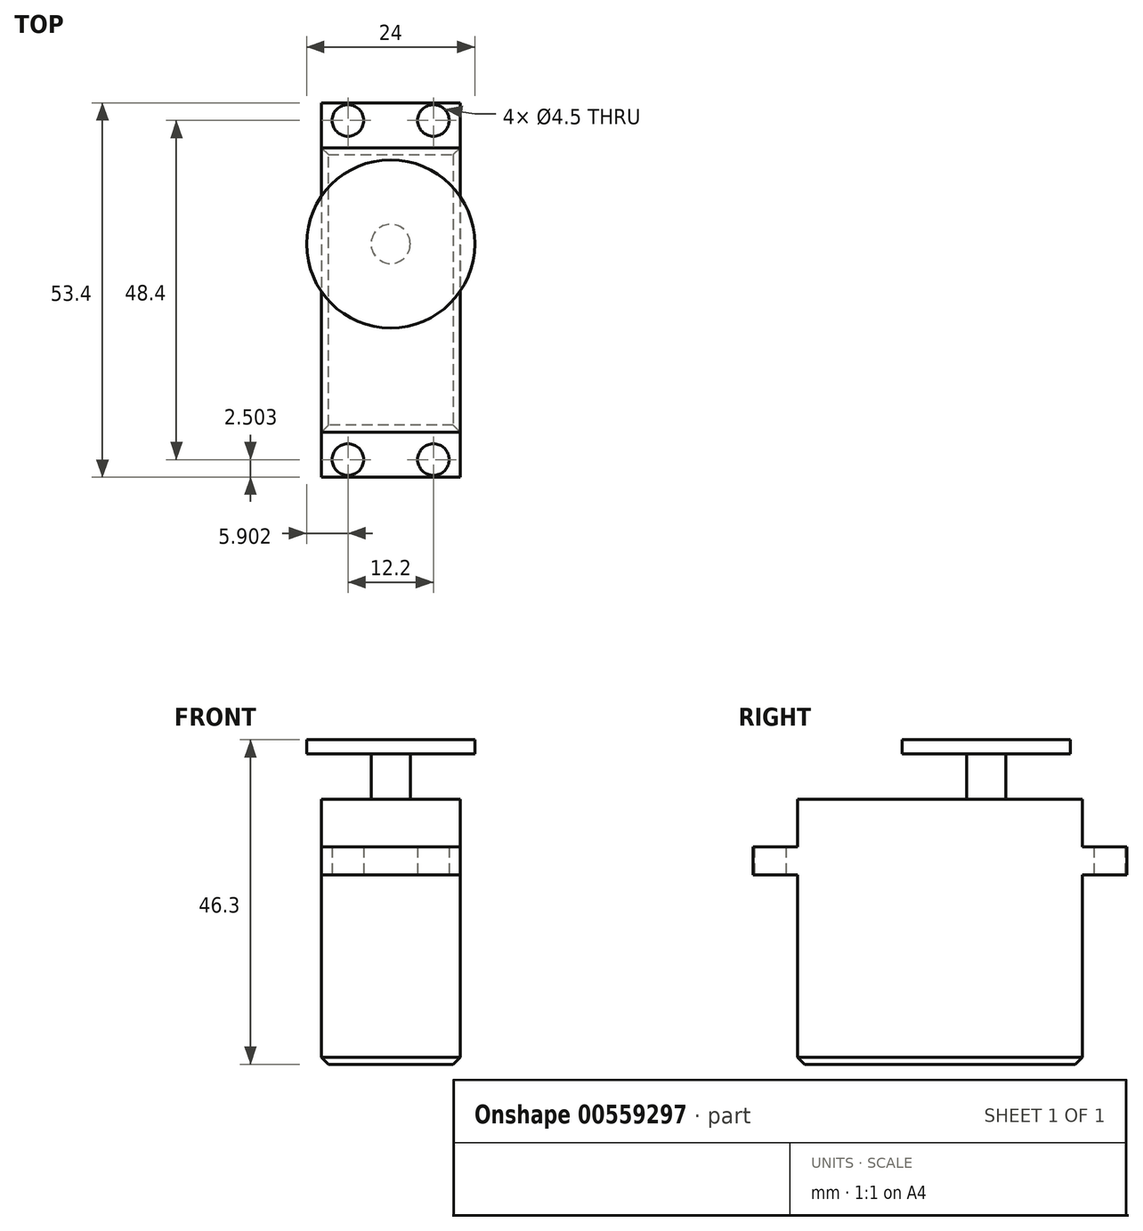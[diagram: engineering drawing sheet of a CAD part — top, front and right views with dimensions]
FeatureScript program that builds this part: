
annotation { "Feature Type Name" : "Feature", "Feature Type Description" : "" }
export const myFeature = defineFeature(function(context is Context, id is Id, definition is map)
    precondition{}
    {
        {
            var Q0;
            Q0=qCreatedBy(makeId("Top.planeOp"),FACE);
            var sketch = newSketch(context, id + "F0", { "sketchPlane" : qUnion([Q0])});
            skLineSegment(sketch, "E0.bottom", {"start": v(-14.2, 14.35) * mm, "end": v(5.6, 14.35) * mm});
            skLineSegment(sketch, "E0.top", {"start": v(-14.2, -26.25) * mm, "end": v(5.6, -26.25) * mm});
            skLineSegment(sketch, "E0.left", {"start": v(-14.2, 14.35) * mm, "end": v(-14.2, -26.25) * mm});
            skLineSegment(sketch, "E0.right", {"start": v(5.6, 14.35) * mm, "end": v(5.6, -26.25) * mm});
            skSolve(sketch);
        }
        {
            var Q0;
            Q0=makeQuery(id+"F0.imprint","IMPRINT",FACE,{"disambiguationData":[TD([[makeQuery(id+"F0.imprint","IMPRINT",EDGE,{"derivedFrom":sQuery(id+"F0.wireOp",EDGE,"E0.bottom")}),-1.0]])]});
            extrude(context, id + "F1", {"entities" : qUnion([Q0]), "depth" : 27 * mm, "offsetDistance" : 25 * mm});
        }
        {
            var Q0;
            Q0=makeQuery(id+"F1.opExtrude","CAP_FACE",FACE,{"disambiguationData":[OSD([sQuery(id+"F0.wireOp",EDGE,"E0.bottom"),sQuery(id+"F0.wireOp",EDGE,"E0.top"),sQuery(id+"F0.wireOp",EDGE,"E0.left"),sQuery(id+"F0.wireOp",EDGE,"E0.right")])],"isStart":false});
            var sketch = newSketch(context, id + "F2", { "sketchPlane" : qUnion([Q0])});
            skLineSegment(sketch, "E1", {"start": v(-14.2, 14.35) * mm, "end": v(-14.2, 20.75) * mm});
            skLineSegment(sketch, "E2", {"start": v(-14.2, 20.75) * mm, "end": v(5.6, 20.75) * mm});
            skLineSegment(sketch, "E3", {"start": v(5.6, 20.75) * mm, "end": v(5.6, 14.35) * mm});
            skLineSegment(sketch, "E4", {"start": v(-14.2, -26.25) * mm, "end": v(-14.2, -32.65) * mm});
            skLineSegment(sketch, "E5", {"start": v(-14.2, -32.65) * mm, "end": v(5.6, -32.65) * mm});
            skLineSegment(sketch, "E6", {"start": v(5.6, -32.65) * mm, "end": v(5.6, -26.25) * mm});
            skLineSegment(sketch, "E7", {"start": v(-14.2, -26.25) * mm, "end": v(5.6, -26.25) * mm});
            skLineSegment(sketch, "E8", {"start": v(-14.2, 14.35) * mm, "end": v(5.6, 14.35) * mm});
            skLineSegment(sketch, "E9", {"start": v(-14.2, 14.35) * mm, "end": v(-14.2, -26.25) * mm});
            skLineSegment(sketch, "E10", {"start": v(5.6, 14.35) * mm, "end": v(5.6, -26.25) * mm});
            skLineSegment(sketch, "E11", {"start": v(-4.3, 20.75) * mm, "end": v(-4.3, 18.25) * mm, "construction": true});
            skLineSegment(sketch, "E12", {"start": v(-4.3, 18.25) * mm, "end": v(-4.3, -30.15) * mm, "construction": true});
            skLineSegment(sketch, "E13", {"start": v(-4.3, -30.15) * mm, "end": v(-4.3, -32.65) * mm, "construction": true});
            skLineSegment(sketch, "E14", {"start": v(-4.3, 18.25) * mm, "end": v(-10.4, 18.25) * mm, "construction": true});
            skLineSegment(sketch, "E15", {"start": v(-10.4, 18.25) * mm, "end": v(-14.2, 18.25) * mm, "construction": true});
            skLineSegment(sketch, "E16", {"start": v(-4.3, 18.25) * mm, "end": v(1.8, 18.25) * mm, "construction": true});
            skLineSegment(sketch, "E17", {"start": v(1.8, 18.25) * mm, "end": v(5.6, 18.25) * mm, "construction": true});
            skCircle(sketch, "E18", {"center": v(-10.4, 18.25) * mm, "radius": 2.25 * mm});
            skCircle(sketch, "E19", {"center": v(1.8, 18.25) * mm, "radius": 2.25 * mm});
            skLineSegment(sketch, "E20", {"start": v(-4.3, -30.15) * mm, "end": v(-10.4, -30.15) * mm, "construction": true});
            skLineSegment(sketch, "E21", {"start": v(-10.4, -30.15) * mm, "end": v(-14.2, -30.15) * mm, "construction": true});
            skLineSegment(sketch, "E22", {"start": v(-4.3, -30.15) * mm, "end": v(1.8, -30.15) * mm, "construction": true});
            skLineSegment(sketch, "E23", {"start": v(1.8, -30.15) * mm, "end": v(5.6, -30.15) * mm, "construction": true});
            skCircle(sketch, "E24", {"center": v(-10.4, -30.15) * mm, "radius": 2.25 * mm});
            skCircle(sketch, "E25", {"center": v(1.8, -30.15) * mm, "radius": 2.25 * mm});
            skSolve(sketch);
        }
        {
            var Q0;
            Q0=makeQuery(id+"F2.imprint","IMPRINT",FACE,{"disambiguationData":[TD([[makeQuery(id+"F2.imprint","IMPRINT",EDGE,{"derivedFrom":sQuery(id+"F2.wireOp",EDGE,"E1")}),-1.0]])]});
            var Q1;
            Q1=makeQuery(id+"F2.imprint","IMPRINT",FACE,{"disambiguationData":[TD([[makeQuery(id+"F2.imprint","IMPRINT",EDGE,{"derivedFrom":sQuery(id+"F2.wireOp",EDGE,"E4")}),1.0]])]});
            extrude(context, id + "F3", {"entities" : qUnion([Q0, Q1]), "operationType" : NewBodyOperationType.ADD, "depth" : 4 * mm, "offsetDistance" : 25 * mm});
        }
        {
            var Q0;
            Q0=makeQuery(id+"F1.opExtrude","CAP_FACE",FACE,{"disambiguationData":[OSD([sQuery(id+"F0.wireOp",EDGE,"E0.bottom"),sQuery(id+"F0.wireOp",EDGE,"E0.top"),sQuery(id+"F0.wireOp",EDGE,"E0.left"),sQuery(id+"F0.wireOp",EDGE,"E0.right")])],"isStart":false});
            extrude(context, id + "F4", {"entities" : qUnion([Q0]), "operationType" : NewBodyOperationType.ADD, "depth" : 10.8 * mm, "offsetDistance" : 25 * mm});
        }
        {
            var Q0;
            Q0=makeQuery(id+"F1.opExtrude","CAP_EDGE",EDGE,{"disambiguationData":[OSD([sQuery(id+"F0.wireOp",EDGE,"E0.left")])],"isStart":true});
            var Q1;
            Q1=makeQuery(id+"F1.opExtrude","CAP_EDGE",EDGE,{"disambiguationData":[OSD([sQuery(id+"F0.wireOp",EDGE,"E0.bottom")])],"isStart":true});
            var Q2;
            Q2=makeQuery(id+"F1.opExtrude","CAP_EDGE",EDGE,{"disambiguationData":[OSD([sQuery(id+"F0.wireOp",EDGE,"E0.right")])],"isStart":true});
            var Q3;
            Q3=makeQuery(id+"F1.opExtrude","CAP_EDGE",EDGE,{"disambiguationData":[OSD([sQuery(id+"F0.wireOp",EDGE,"E0.top")])],"isStart":true});
            chamfer(context, id + "F5", {"entities" : qUnion([Q0, Q1, Q2, Q3]), "width" : 1 * mm, "tangentPropagation" : true});
        }
        {
            var Q0;
            Q0=makeQuery(id+"F4.opExtrude","CAP_FACE",FACE,{"disambiguationData":[OSD([sQuery(id+"F0.wireOp",EDGE,"E0.bottom"),sQuery(id+"F0.wireOp",EDGE,"E0.top"),sQuery(id+"F0.wireOp",EDGE,"E0.left"),sQuery(id+"F0.wireOp",EDGE,"E0.right")])],"isStart":false});
            var sketch = newSketch(context, id + "F6", { "sketchPlane" : qUnion([Q0])});
            skLineSegment(sketch, "E26", {"start": v(-4.3, 14.35) * mm, "end": v(-4.3, 0.64) * mm, "construction": true});
            skCircle(sketch, "E27", {"center": v(-4.3, 0.64) * mm, "radius": 2.8 * mm});
            skSolve(sketch);
        }
        {
            var Q0;
            Q0=makeQuery(id+"F6.imprint","IMPRINT",FACE,{"disambiguationData":[TD([[makeQuery(id+"F6.imprint","IMPRINT",EDGE,{"derivedFrom":sQuery(id+"F6.wireOp",EDGE,"E27")}),1.0]])]});
            extrude(context, id + "F7", {"entities" : qUnion([Q0]), "operationType" : NewBodyOperationType.ADD, "depth" : 6.5 * mm, "offsetDistance" : 25 * mm});
        }
        {
            var Q0;
            Q0=makeQuery(id+"F7.opExtrude","CAP_FACE",FACE,{"disambiguationData":[OSD([sQuery(id+"F6.wireOp",EDGE,"E27")])],"isStart":false});
            var sketch = newSketch(context, id + "F8", { "sketchPlane" : qUnion([Q0])});
            skCircle(sketch, "E28", {"center": v(-4.3, 0.64) * mm, "radius": 12 * mm});
            skSolve(sketch);
        }
        {
            var Q0;
            Q0=makeQuery(id+"F8.imprint","IMPRINT",FACE,{"disambiguationData":[TD([[makeQuery(id+"F8.imprint","IMPRINT",EDGE,{"derivedFrom":sQuery(id+"F8.wireOp",EDGE,"E28")}),1.0]])]});
            var Q1;
            Q1=makeQuery(id+"F8.imprint","IMPRINT",FACE,{"disambiguationData":[TD([[makeQuery(id+"F8.imprint","IMPRINT",EDGE,{"derivedFrom":makeQuery(id+"F7.opExtrude","CAP_EDGE",EDGE,{"disambiguationData":[OSD([sQuery(id+"F6.wireOp",EDGE,"E27")])],"isStart":false})}),1.0]])]});
            extrude(context, id + "F9", {"entities" : qUnion([Q0, Q1]), "operationType" : NewBodyOperationType.ADD, "depth" : 2 * mm, "offsetDistance" : 25 * mm});
        }
    });
